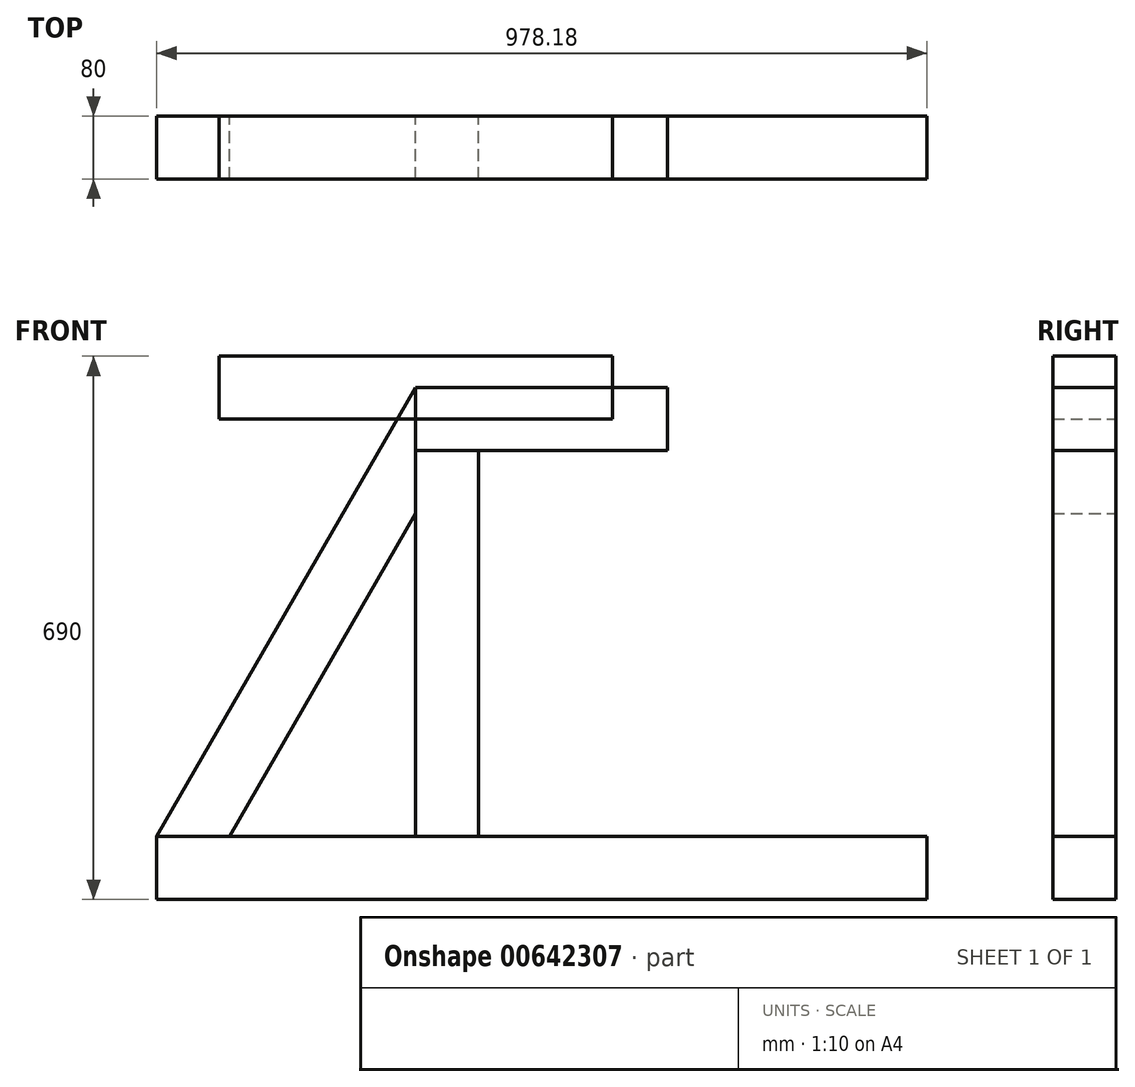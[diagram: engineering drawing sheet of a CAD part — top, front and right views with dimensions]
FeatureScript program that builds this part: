
annotation { "Feature Type Name" : "Feature", "Feature Type Description" : "" }
export const myFeature = defineFeature(function(context is Context, id is Id, definition is map)
    precondition{}
    {
        {
            var Q0;
            Q0=qCreatedBy(makeId("Front.planeOp"),FACE);
            var sketch = newSketch(context, id + "F0", { "sketchPlane" : qUnion([Q0])});
            skLineSegment(sketch, "E0.bottom", {"start": v(250, -40) * mm, "end": v(-250, -40) * mm});
            skLineSegment(sketch, "E0.top", {"start": v(250, 40) * mm, "end": v(-250, 40) * mm});
            skLineSegment(sketch, "E0.left", {"start": v(250, -40) * mm, "end": v(250, 40) * mm});
            skLineSegment(sketch, "E0.right", {"start": v(-250, -40) * mm, "end": v(-250, 40) * mm});
            skPoint(sketch, "E0.middle", {"position": v(0, 0) * mm});
            skSolve(sketch);
        }
        {
            var Q0;
            Q0=makeQuery(id+"F0.imprint","IMPRINT",FACE,{"disambiguationData":[TD([[makeQuery(id+"F0.imprint","IMPRINT",EDGE,{"derivedFrom":sQuery(id+"F0.wireOp",EDGE,"E0.bottom")}),-1.0]])]});
            extrude(context, id + "F1", {"entities" : qUnion([Q0]), "depth" : 80 * mm, "offsetDistance" : 25 * mm});
        }
        {
            var Q0;
            Q0=qCreatedBy(makeId("Front.planeOp"),FACE);
            var sketch = newSketch(context, id + "F2", { "sketchPlane" : qUnion([Q0])});
            skLineSegment(sketch, "E1", {"start": v(0, 0) * mm, "end": v(320, 0) * mm});
            skLineSegment(sketch, "E2", {"start": v(320, 0) * mm, "end": v(320, -80) * mm});
            skLineSegment(sketch, "E3", {"start": v(320, -80) * mm, "end": v(0, -80) * mm});
            skLineSegment(sketch, "E4", {"start": v(0, -80) * mm, "end": v(0, 0) * mm});
            skLineSegment(sketch, "E5.bottom", {"start": v(-329.09, -570) * mm, "end": v(649.09, -570) * mm});
            skLineSegment(sketch, "E5.top", {"start": v(-329.09, -650) * mm, "end": v(649.09, -650) * mm});
            skLineSegment(sketch, "E5.left", {"start": v(-329.09, -570) * mm, "end": v(-329.09, -650) * mm});
            skLineSegment(sketch, "E5.right", {"start": v(649.09, -570) * mm, "end": v(649.09, -650) * mm});
            skPoint(sketch, "E6", {"position": v(160, -570) * mm});
            skLineSegment(sketch, "E7", {"start": v(160, -80) * mm, "end": v(160, -570) * mm, "construction": true});
            skLineSegment(sketch, "E8", {"start": v(320, 0) * mm, "end": v(649.09, -570) * mm});
            skLineSegment(sketch, "E9", {"start": v(556.71, -570) * mm, "end": v(320, -160) * mm});
            skLineSegment(sketch, "E10", {"start": v(320, -160) * mm, "end": v(320, -80) * mm});
            skLineSegment(sketch, "E11", {"start": v(320, -160) * mm, "end": v(320, -570) * mm});
            skLineSegment(sketch, "E12", {"start": v(240, -80) * mm, "end": v(240, -570) * mm});
            skLineSegment(sketch, "E13", {"start": v(0, -80) * mm, "end": v(0, -570) * mm});
            skLineSegment(sketch, "E14", {"start": v(80, -80) * mm, "end": v(80, -570) * mm});
            skLineSegment(sketch, "E15", {"start": v(0, 0) * mm, "end": v(-329.09, -570) * mm});
            skLineSegment(sketch, "E16", {"start": v(0, -160) * mm, "end": v(-236.71, -570) * mm});
            skSolve(sketch);
        }
        {
            var Q0;
            Q0=makeQuery(id+"F2.imprint","IMPRINT",FACE,{"disambiguationData":[TD([[makeQuery(id+"F2.imprint","IMPRINT",EDGE,{"derivedFrom":sQuery(id+"F2.wireOp",EDGE,"E5.top")}),1.0]])]});
            extrude(context, id + "F3", {"entities" : qUnion([Q0]), "depth" : 80 * mm, "offsetDistance" : 25 * mm});
        }
        {
            var Q0;
            Q0=makeQuery(id+"F2.imprint","IMPRINT",FACE,{"disambiguationData":[TD([[makeQuery(id+"F2.imprint","IMPRINT",EDGE,{"derivedFrom":sQuery(id+"F2.wireOp",EDGE,"E1")}),-1.0]])]});
            extrude(context, id + "F4", {"entities" : qUnion([Q0]), "depth" : 80 * mm, "offsetDistance" : 25 * mm});
        }
        {
            var Q0;
            {var subQ6=sQuery(id+"F2.wireOp",EDGE,"E14");Q0=makeQuery(id+"F2.imprint","IMPRINT",FACE,{"disambiguationData":[TD([[makeQuery(id+"F2.imprint","IMPRINT",EDGE,{"derivedFrom":subQ6}),-1.0]])]});}
            extrude(context, id + "F5", {"entities" : qUnion([Q0]), "depth" : 80 * mm, "offsetDistance" : 25 * mm});
        }
        {
            var Q0;
            {var subQ2=sQuery(id+"F2.wireOp",EDGE,"E4");Q0=makeQuery(id+"F2.imprint","IMPRINT",FACE,{"disambiguationData":[TD([[makeQuery(id+"F2.imprint","IMPRINT",EDGE,{"derivedFrom":subQ2}),1.0]])]});}
            extrude(context, id + "F6", {"entities" : qUnion([Q0]), "depth" : 80 * mm, "offsetDistance" : 25 * mm});
        }
    });
